# Revit family: PLAFOLED CARRÉ
name_source: partatom
category: Luminaires
units: mm (PartAtom-declared; Revit-internal decimal feet)

## family parameters
Cote de connecteur circulaire = Utiliser le diamètre
Couper avec des vides une fois chargée = Oui
Hôte = Face
Numéro OmniClass = 23.80.70.11.14.11
Partagée = Oui
Point de calcul de pièce = Oui
Source d'éclairage = Oui
Titre OmniClass = Downlights
Type d'élément = Normal

## types (8) — shared parameters
Angle de l'inclinaison = 60.00°
Distance fond réflecteur = 33 mm  [stored 0.108268 ft]
Emettre la visibilité des formes dans le rendu = Non
Emettre à partir de la largeur du rectangle = 610 mm
Emettre à partir de la longueur du rectangle = 1219 mm
Fabricant = Résistex
Filtre de couleur = 16777215
Garantie = 5 ans
Gradation des changements de température de couleur de lampe = <Aucun>
IK = 08
IP = 40
Image du type = <Aucun>
Indice de charge = Eclairage
Largeur diffuseur = 192 mm  [stored 0.629921 ft]
Longueur diffuseur = 192 mm  [stored 0.629921 ft]
Matériau diffuseur = PC Transparent
Modèle = Plafoled
Nombre pôles = 1
Tension = 230 V
URL = https://www.resistex-sa.com
Épaisseur = 35 mm  [stored 0.114829 ft]
Épaisseur diffuseur = 2 mm  [stored 0.00656168 ft]
zero-valued in all types: Elévation par défaut

## per-type parameters (varying)
| type | Charge apparente | Commentaires relatifs à la puissance | Coût | Description | Fichier de distribution photométrique | Largeur | Longueur | Matériau corps |
| 749203 | 20 VA | 18.8W | 70 $ | Plafonnier équipé d'un module LED SMD, efficacité lumineuse de 75.4lm/W | 749203.ies | 240 mm  [stored 0.787402 ft] | 240 mm  [stored 0.787402 ft] | PC Blanc |
| 749293 | 20 VA | 18.8W | 70 $ | Plafonnier équipé d'un module LED SMD, efficacité lumineuse de 75.4lm/W | 749293.ies | 240 mm  [stored 0.787402 ft] | 240 mm  [stored 0.787402 ft] | PC Noir |
| 749204 | 20 VA | 18.8W | 70 $ | Plafonnier équipé d'un module LED SMD, efficacité lumineuse de 80.9lm/W | 749204.ies | 240 mm  [stored 0.787402 ft] | 240 mm  [stored 0.787402 ft] | PC Blanc |
| 749294 | 20 VA | 18.8W | 70 $ | Plafonnier équipé d'un module LED SMD, efficacité lumineuse de 80.9lm/W | 749294.ies | 240 mm  [stored 0.787402 ft] | 240 mm  [stored 0.787402 ft] | PC Noir |
| 749363 | 34 VA | 33.6W | 115 $ | Plafonnier équipé d'un module LED SMD, efficacité lumineuse de 77.1lm/W | 749363.ies | 320 mm  [stored 1.04987 ft] | 320 mm  [stored 1.04987 ft] | PC Blanc |
| 749393 | 34 VA | 33.6W | 115 $ | Plafonnier équipé d'un module LED SMD, efficacité lumineuse de 77.1lm/W | 749393.ies | 320 mm  [stored 1.04987 ft] | 320 mm  [stored 1.04987 ft] | PC Noir |
| 749364 | 34 VA | 33.6W | 115 $ | Plafonnier équipé d'un module LED SMD, efficacité lumineuse de 81.2lm/W | 749364.ies | 320 mm  [stored 1.04987 ft] | 320 mm  [stored 1.04987 ft] | PC Blanc |
| 749394 | 34 VA | 33.6W | 115 $ | Plafonnier équipé d'un module LED SMD, efficacité lumineuse de 81.2lm/W | 749394.ies | 320 mm  [stored 1.04987 ft] | 320 mm  [stored 1.04987 ft] | PC Noir |

note: [stored X ft] marks values corroborated as IEEE doubles in the binary element streams (Revit-internal decimal feet)
